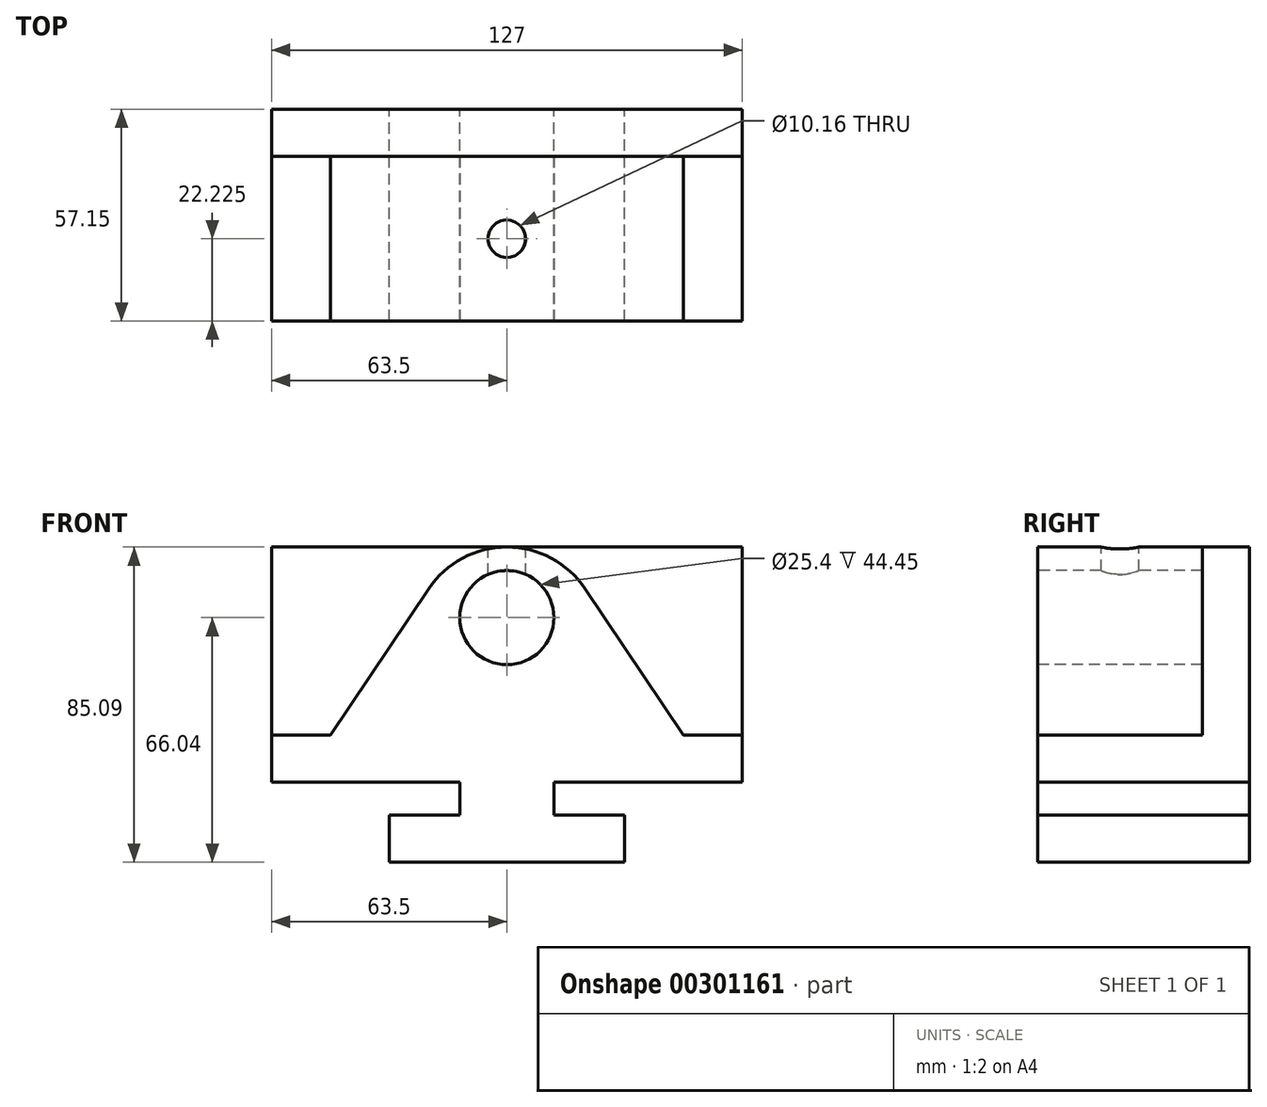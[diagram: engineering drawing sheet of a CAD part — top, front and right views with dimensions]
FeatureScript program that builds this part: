
annotation { "Feature Type Name" : "Feature", "Feature Type Description" : "" }
export const myFeature = defineFeature(function(context is Context, id is Id, definition is map)
    precondition{}
    {
        {
            var Q0;
            Q0=qCreatedBy(makeId("Front.planeOp"),FACE);
            var sketch = newSketch(context, id + "F0", { "sketchPlane" : qUnion([Q0])});
            skLineSegment(sketch, "E0", {"start": v(0, 0) * mm, "end": v(31.75, 0) * mm});
            skLineSegment(sketch, "E1", {"start": v(0, 0) * mm, "end": v(-31.75, 0) * mm});
            skLineSegment(sketch, "E2", {"start": v(31.75, 0) * mm, "end": v(31.75, 12.7) * mm});
            skLineSegment(sketch, "E3", {"start": v(31.75, 12.7) * mm, "end": v(12.7, 12.7) * mm});
            skLineSegment(sketch, "E4", {"start": v(-31.75, 0) * mm, "end": v(-31.75, 12.7) * mm});
            skLineSegment(sketch, "E5", {"start": v(-31.75, 12.7) * mm, "end": v(-12.7, 12.7) * mm});
            skLineSegment(sketch, "E6", {"start": v(-12.7, 12.7) * mm, "end": v(-12.7, 21.6) * mm});
            skLineSegment(sketch, "E7", {"start": v(12.7, 21.59) * mm, "end": v(12.7, 12.7) * mm});
            skLineSegment(sketch, "E8", {"start": v(0, 85.1) * mm, "end": v(63.5, 85.1) * mm});
            skLineSegment(sketch, "E9", {"start": v(0, 85.1) * mm, "end": v(-63.5, 85.1) * mm});
            skLineSegment(sketch, "E10", {"start": v(-63.5, 85.1) * mm, "end": v(-63.5, 21.6) * mm});
            skLineSegment(sketch, "E11", {"start": v(-63.5, 21.6) * mm, "end": v(-12.7, 21.6) * mm});
            skLineSegment(sketch, "E12", {"start": v(63.5, 85.1) * mm, "end": v(63.5, 21.6) * mm});
            skLineSegment(sketch, "E13", {"start": v(63.5, 21.6) * mm, "end": v(12.7, 21.59) * mm});
            skSolve(sketch);
        }
        {
            var Q0;
            Q0 = qSketchRegion(id + "F0", true);
            extrude(context, id + "F1", {"entities" : qUnion([Q0]), "depth" : 57.15 * mm});
        }
        {
            var Q0;
            Q0=makeQuery(id+"F1.opExtrude","CAP_FACE",FACE,{"disambiguationData":[OSD([sQuery(id+"F0.wireOp",EDGE,"E0"),sQuery(id+"F0.wireOp",EDGE,"E1"),sQuery(id+"F0.wireOp",EDGE,"E2"),sQuery(id+"F0.wireOp",EDGE,"E3"),sQuery(id+"F0.wireOp",EDGE,"E4"),sQuery(id+"F0.wireOp",EDGE,"E5"),sQuery(id+"F0.wireOp",EDGE,"E6"),sQuery(id+"F0.wireOp",EDGE,"E7"),sQuery(id+"F0.wireOp",EDGE,"E8"),sQuery(id+"F0.wireOp",EDGE,"E9"),sQuery(id+"F0.wireOp",EDGE,"E10"),sQuery(id+"F0.wireOp",EDGE,"E11"),sQuery(id+"F0.wireOp",EDGE,"E12"),sQuery(id+"F0.wireOp",EDGE,"E13")])],"isStart":false});
            var sketch = newSketch(context, id + "F2", { "sketchPlane" : qUnion([Q0])});
            skLineSegment(sketch, "E14", {"start": v(-63.5, 34.3) * mm, "end": v(-47.62, 34.3) * mm});
            skLineSegment(sketch, "E15", {"start": v(47.62, 34.3) * mm, "end": v(63.5, 34.3) * mm});
            skLineSegment(sketch, "E16", {"start": v(-47.62, 34.3) * mm, "end": v(-21.1, 73.84) * mm});
            skLineSegment(sketch, "E17", {"start": v(21.1, 73.84) * mm, "end": v(47.62, 34.3) * mm});
            skArc(sketch, "E18", {"start": v(-21.1, 73.84) * mm, "mid": v(0, 85.1) * mm, "end": v(21.1, 73.84) * mm});
            skSolve(sketch);
        }
        {
            var Q0;
            Q0 = qSketchRegion(id + "F2", true);
            var Q1;
            {var subQ6=sQuery(id+"F2.wireOp",EDGE,"E14");Q1=makeQuery(id+"F2.imprint","IMPRINT",FACE,{"disambiguationData":[TD([[makeQuery(id+"F2.imprint","IMPRINT",EDGE,{"derivedFrom":subQ6}),1.0]])]});}
            var Q2;
            {var subQ6=sQuery(id+"F2.wireOp",EDGE,"E15");Q2=makeQuery(id+"F2.imprint","IMPRINT",FACE,{"disambiguationData":[TD([[makeQuery(id+"F2.imprint","IMPRINT",EDGE,{"derivedFrom":subQ6}),1.0]])]});}
            extrude(context, id + "F3", {"entities" : qUnion([Q0, Q1, Q2]), "operationType" : NewBodyOperationType.REMOVE, "oppositeDirection" : true, "depth" : 44.45 * mm});
        }
        {
            var Q0;
            Q0=makeQuery(id+"F1.opExtrude","CAP_FACE",FACE,{"disambiguationData":[OSD([sQuery(id+"F0.wireOp",EDGE,"E0"),sQuery(id+"F0.wireOp",EDGE,"E1"),sQuery(id+"F0.wireOp",EDGE,"E2"),sQuery(id+"F0.wireOp",EDGE,"E3"),sQuery(id+"F0.wireOp",EDGE,"E4"),sQuery(id+"F0.wireOp",EDGE,"E5"),sQuery(id+"F0.wireOp",EDGE,"E6"),sQuery(id+"F0.wireOp",EDGE,"E7"),sQuery(id+"F0.wireOp",EDGE,"E8"),sQuery(id+"F0.wireOp",EDGE,"E9"),sQuery(id+"F0.wireOp",EDGE,"E10"),sQuery(id+"F0.wireOp",EDGE,"E11"),sQuery(id+"F0.wireOp",EDGE,"E12"),sQuery(id+"F0.wireOp",EDGE,"E13")])],"isStart":false});
            var sketch = newSketch(context, id + "F4", { "sketchPlane" : qUnion([Q0])});
            skCircle(sketch, "E19", {"center": v(0, 66.04) * mm, "radius": 12.7 * mm});
            skSolve(sketch);
        }
        {
            var Q0;
            Q0 = qSketchRegion(id + "F4", true);
            extrude(context, id + "F5", {"entities" : qUnion([Q0]), "operationType" : NewBodyOperationType.REMOVE, "oppositeDirection" : true, "depth" : 44.45 * mm});
        }
        {
            var Q0;
            Q0=makeQuery(id+"F1.opExtrude","SWEPT_FACE",FACE,{"disambiguationData":[OSD([sQuery(id+"F0.wireOp",EDGE,"E8"),sQuery(id+"F0.wireOp",EDGE,"E9")])]});
            var sketch = newSketch(context, id + "F6", { "sketchPlane" : qUnion([Q0])});
            skCircle(sketch, "E20", {"center": v(0, -34.93) * mm, "radius": 5.08 * mm});
            skSolve(sketch);
        }
        {
            var Q0;
            Q0 = qSketchRegion(id + "F6", true);
            extrude(context, id + "F7", {"entities" : qUnion([Q0]), "operationType" : NewBodyOperationType.REMOVE, "oppositeDirection" : true, "depth" : 25.4 * mm});
        }
    });
